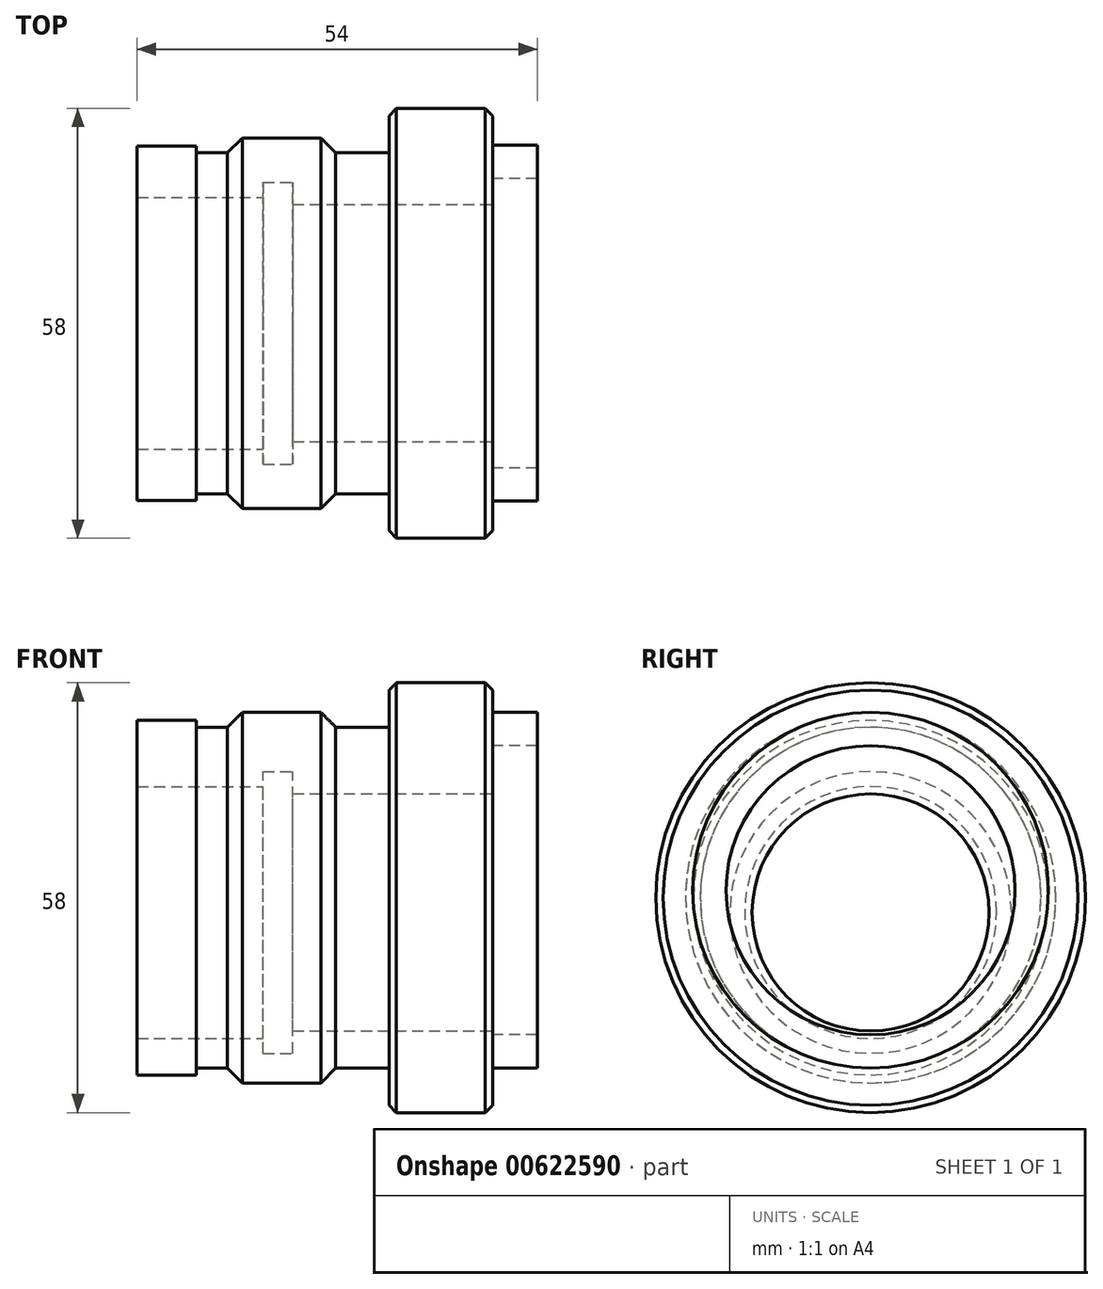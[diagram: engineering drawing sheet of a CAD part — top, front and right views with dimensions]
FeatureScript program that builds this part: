
annotation { "Feature Type Name" : "Feature", "Feature Type Description" : "" }
export const myFeature = defineFeature(function(context is Context, id is Id, definition is map)
    precondition{}
    {
        {
            var Q0;
            Q0=qCreatedBy(makeId("Front.planeOp"),FACE);
            var sketch = newSketch(context, id + "F0", { "sketchPlane" : qUnion([Q0])});
            skLineSegment(sketch, "E0", {"start": v(-4.34, 0) * mm, "end": v(56.52, 0) * mm, "construction": true});
            skLineSegment(sketch, "E1", {"start": v(0, 0) * mm, "end": v(0, 23.92) * mm});
            skLineSegment(sketch, "E2", {"start": v(0, 23.92) * mm, "end": v(8, 23.92) * mm});
            skLineSegment(sketch, "E3", {"start": v(8, 23.92) * mm, "end": v(8, 23) * mm});
            skLineSegment(sketch, "E4", {"start": v(8, 23) * mm, "end": v(12, 23) * mm});
            skLineSegment(sketch, "E5", {"start": v(12, 23) * mm, "end": v(12, 25) * mm});
            skLineSegment(sketch, "E6", {"start": v(12, 25) * mm, "end": v(27, 25) * mm});
            skLineSegment(sketch, "E7", {"start": v(27, 25) * mm, "end": v(27, 23) * mm});
            skLineSegment(sketch, "E8", {"start": v(27, 23) * mm, "end": v(34, 23) * mm});
            skLineSegment(sketch, "E9", {"start": v(34, 23) * mm, "end": v(34, 29) * mm});
            skLineSegment(sketch, "E10", {"start": v(34, 29) * mm, "end": v(48, 29) * mm});
            skLineSegment(sketch, "E11", {"start": v(48, 29) * mm, "end": v(48, 0) * mm});
            skLineSegment(sketch, "E12", {"start": v(48, 0) * mm, "end": v(0, 0) * mm});
            skSolve(sketch);
        }
        {
            var Q0;
            Q0 = qSketchRegion(id + "F0", true);
            var Q1;
            Q1=sQuery(id+"F0.wireOp",EDGE,"E0");
            revolve(context, id + "F1", {"entities" : qUnion([Q0]), "axis" : qUnion([Q1]), "revolveType" : RevolveType.FULL});
        }
        {
            var Q0;
            Q0=makeQuery(id+"F1.opRevolve","SWEPT_EDGE",EDGE,{"disambiguationData":[OSD([sQuery(id+"F0.wireOp",EDGE,"E6"),sQuery(id+"F0.wireOp",EDGE,"E7")])]});
            var Q1;
            Q1=makeQuery(id+"F1.opRevolve","SWEPT_EDGE",EDGE,{"disambiguationData":[OSD([sQuery(id+"F0.wireOp",EDGE,"E5"),sQuery(id+"F0.wireOp",EDGE,"E6")])]});
            chamfer(context, id + "F2", {"entities" : qUnion([Q0, Q1]), "width" : 2.2 * mm, "tangentPropagation" : true});
        }
        {
            var Q0;
            Q0=makeQuery(id+"F1.opRevolve","SWEPT_EDGE",EDGE,{"disambiguationData":[OSD([sQuery(id+"F0.wireOp",EDGE,"E9"),sQuery(id+"F0.wireOp",EDGE,"E10")])]});
            var Q1;
            Q1=makeQuery(id+"F1.opRevolve","SWEPT_EDGE",EDGE,{"disambiguationData":[OSD([sQuery(id+"F0.wireOp",EDGE,"E10"),sQuery(id+"F0.wireOp",EDGE,"E11")])]});
            chamfer(context, id + "F3", {"entities" : qUnion([Q0, Q1]), "width" : 1 * mm, "tangentPropagation" : true});
        }
        {
            var Q0;
            Q0=makeQuery(id+"F1.opRevolve","SWEPT_FACE",FACE,{"disambiguationData":[OSD([sQuery(id+"F0.wireOp",EDGE,"E11")])]});
            var sketch = newSketch(context, id + "F4", { "sketchPlane" : qUnion([Q0])});
            skCircle(sketch, "E13", {"center": v(0, 1) * mm, "radius": 24 * mm});
            skCircle(sketch, "E14", {"center": v(0, 1) * mm, "radius": 19.5 * mm});
            skSolve(sketch);
        }
        {
            var Q0;
            Q0=makeQuery(id+"F4.imprint","IMPRINT",FACE,{"disambiguationData":[TD([[makeQuery(id+"F4.imprint","IMPRINT",EDGE,{"derivedFrom":sQuery(id+"F4.wireOp",EDGE,"E13")}),1.0]])]});
            extrude(context, id + "F5", {"entities" : qUnion([Q0]), "operationType" : NewBodyOperationType.ADD, "depth" : 6 * mm, "offsetDistance" : 25 * mm});
        }
        {
            var Q0;
            Q0=qCreatedBy(makeId("Front.planeOp"),FACE);
            var sketch = newSketch(context, id + "F6", { "sketchPlane" : qUnion([Q0])});
            skLineSegment(sketch, "E15", {"start": v(-19.88, -2) * mm, "end": v(63, -2) * mm, "construction": true});
            skLineSegment(sketch, "E16", {"start": v(0, -2) * mm, "end": v(0, 15) * mm});
            skLineSegment(sketch, "E17", {"start": v(0, 15) * mm, "end": v(17, 15) * mm});
            skLineSegment(sketch, "E18", {"start": v(17, 15) * mm, "end": v(17, 17) * mm});
            skLineSegment(sketch, "E19", {"start": v(17, 17) * mm, "end": v(21, 17) * mm});
            skLineSegment(sketch, "E20", {"start": v(21, 17) * mm, "end": v(21, 14) * mm});
            skLineSegment(sketch, "E21", {"start": v(21, 14) * mm, "end": v(48, 14) * mm});
            skLineSegment(sketch, "E22", {"start": v(48, 14) * mm, "end": v(48, -2) * mm});
            skLineSegment(sketch, "E23", {"start": v(48, -2) * mm, "end": v(0, -2) * mm});
            skSolve(sketch);
        }
        {
            var Q0;
            Q0 = qSketchRegion(id + "F6", true);
            var Q1;
            Q1=sQuery(id+"F6.wireOp",EDGE,"E15");
            revolve(context, id + "F7", {"operationType" : NewBodyOperationType.REMOVE, "entities" : qUnion([Q0]), "axis" : qUnion([Q1]), "revolveType" : RevolveType.FULL, "oppositeDirection" : true});
        }
    });
